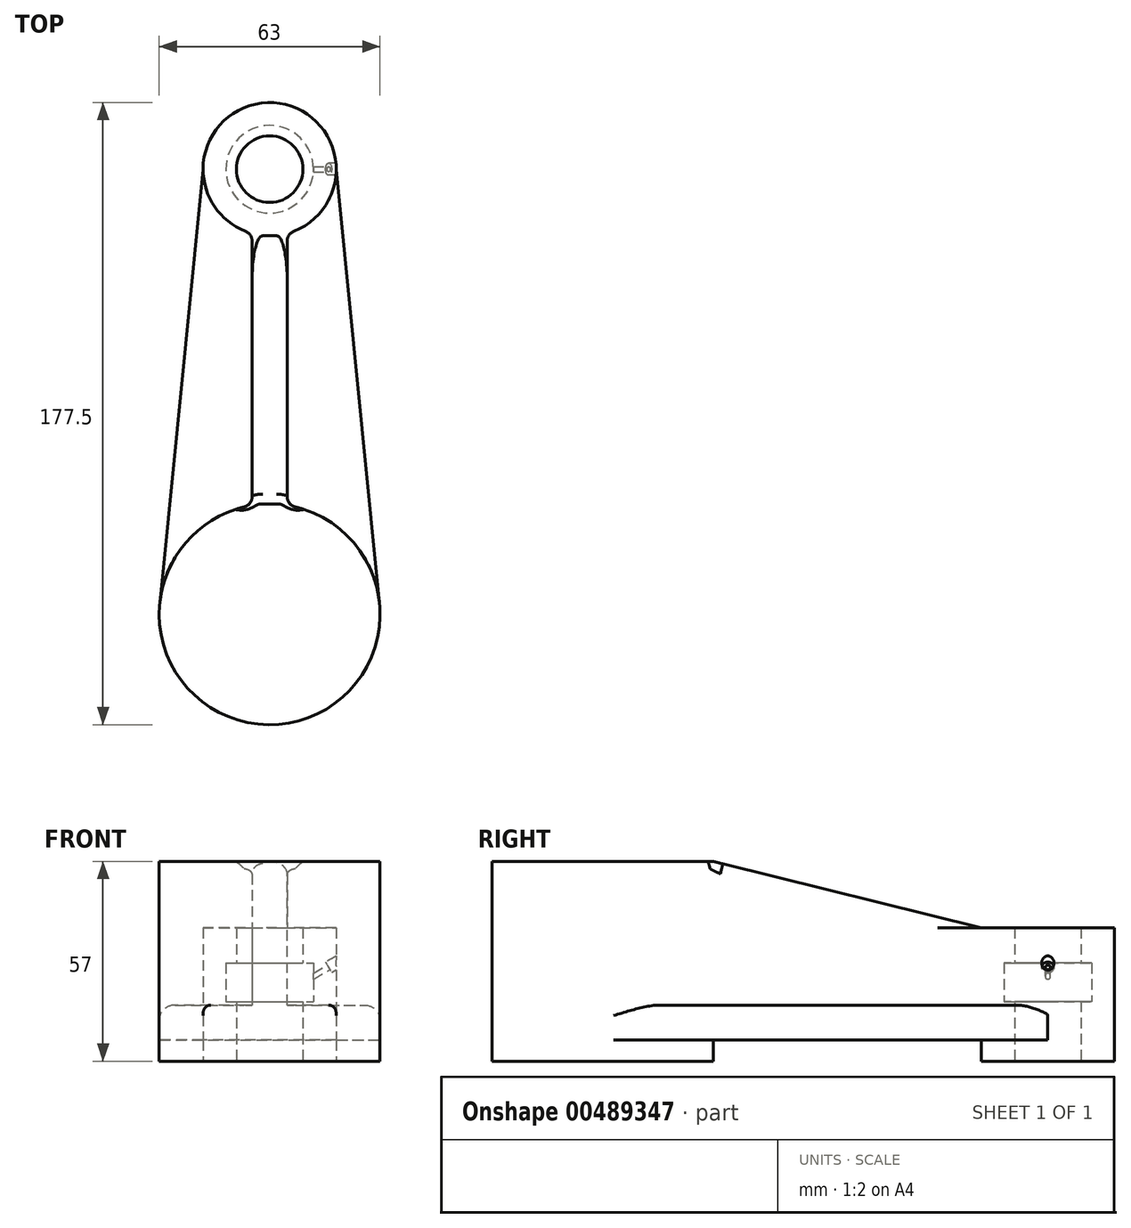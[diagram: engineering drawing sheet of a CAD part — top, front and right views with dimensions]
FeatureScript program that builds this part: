
annotation { "Feature Type Name" : "Feature", "Feature Type Description" : "" }
export const myFeature = defineFeature(function(context is Context, id is Id, definition is map)
    precondition{}
    {
        {
            var Q0;
            Q0=qCreatedBy(makeId("Right.planeOp"),FACE);
            var sketch = newSketch(context, id + "F0", { "sketchPlane" : qUnion([Q0])});
            skLineSegment(sketch, "E0.bottom", {"start": v(0, 0) * mm, "end": v(-19, 0) * mm});
            skLineSegment(sketch, "E0.top", {"start": v(0, 38) * mm, "end": v(-19, 38) * mm});
            skLineSegment(sketch, "E0.right", {"start": v(-19, 0) * mm, "end": v(-19, 38) * mm});
            skLineSegment(sketch, "E1.bottom", {"start": v(-9.5, 28) * mm, "end": v(-12.5, 28) * mm});
            skLineSegment(sketch, "E1.top", {"start": v(-9.5, 17) * mm, "end": v(-12.5, 17) * mm});
            skLineSegment(sketch, "E1.right", {"start": v(-12.5, 28) * mm, "end": v(-12.5, 17) * mm});
            skLineSegment(sketch, "E2.right", {"start": v(-9.5, 0) * mm, "end": v(-9.5, 17) * mm});
            skLineSegment(sketch, "E3.trimOffspring", {"start": v(-9.5, 28) * mm, "end": v(-9.5, 38) * mm});
            skLineSegment(sketch, "E4", {"start": v(0, 0) * mm, "end": v(0, 38) * mm});
            skLineSegment(sketch, "E5", {"start": v(0, 6) * mm, "end": v(-127, 6) * mm});
            skLineSegment(sketch, "E6.bottom", {"start": v(-127, 0) * mm, "end": v(-95.5, 0) * mm});
            skLineSegment(sketch, "E6.top", {"start": v(-127, 57) * mm, "end": v(-95.5, 57) * mm});
            skLineSegment(sketch, "E6.left", {"start": v(-127, 0) * mm, "end": v(-127, 57) * mm});
            skLineSegment(sketch, "E6.right", {"start": v(-95.5, 0) * mm, "end": v(-95.5, 57) * mm});
            skLineSegment(sketch, "E7", {"start": v(-95.5, 57) * mm, "end": v(-19, 38) * mm});
            skLineSegment(sketch, "E8.bottom", {"start": v(-127, 0) * mm, "end": v(-108, 0) * mm});
            skLineSegment(sketch, "E8.top", {"start": v(-127, 57) * mm, "end": v(-108, 57) * mm});
            skLineSegment(sketch, "E8.left", {"start": v(-127, 0) * mm, "end": v(-127, 57) * mm, "construction": true});
            skLineSegment(sketch, "E8.right", {"start": v(-108, 0) * mm, "end": v(-108, 57) * mm});
            skSolve(sketch);
        }
        {
            var Q0;
            {var subQ5=sQuery(id+"F0.wireOp",EDGE,"E6.top");Q0=makeQuery(id+"F0.imprint","IMPRINT",FACE,{"disambiguationData":[TD([[makeQuery(id+"F0.imprint","IMPRINT",EDGE,{"derivedFrom":subQ5}),-1.0]])]});}
            var Q1;
            {var subQ5=sQuery(id+"F0.wireOp",EDGE,"E6.bottom");Q1=makeQuery(id+"F0.imprint","IMPRINT",FACE,{"disambiguationData":[TD([[makeQuery(id+"F0.imprint","IMPRINT",EDGE,{"derivedFrom":subQ5}),1.0]])]});}
            var Q2;
            Q2=sQuery(id+"F0.wireOp",EDGE,"E6.left");
            revolve(context, id + "F1", {"entities" : qUnion([Q0, Q1]), "axis" : qUnion([Q2]), "revolveType" : RevolveType.FULL});
        }
        {
            var Q0;
            {var subQ5=sQuery(id+"F0.wireOp",EDGE,"E6.top");Q0=makeQuery(id+"F0.imprint","IMPRINT",FACE,{"disambiguationData":[TD([[makeQuery(id+"F0.imprint","IMPRINT",EDGE,{"derivedFrom":subQ5}),-1.0]])]});}
            var Q1;
            {var subQ0=sQuery(id+"F0.wireOp",EDGE,"E7");Q1=makeQuery(id+"F0.imprint","IMPRINT",FACE,{"disambiguationData":[TD([[makeQuery(id+"F0.imprint","IMPRINT",EDGE,{"derivedFrom":subQ0}),-1.0]])]});}
            var Q2;
            Q2=makeQuery(id+"F0.imprint","IMPRINT",FACE,{"disambiguationData":[TD([[makeQuery(id+"F0.imprint","IMPRINT",EDGE,{"derivedFrom":sQuery(id+"F0.wireOp",EDGE,"E1.bottom")}),-1.0]])]});
            extrude(context, id + "F2", {"entities" : qUnion([Q0, Q1, Q2]), "operationType" : NewBodyOperationType.ADD, "endBound" : BoundingType.SYMMETRIC, "depth" : 10 * mm, "offsetDistance" : 25 * mm});
        }
        {
            var Q0;
            Q0=makeQuery(id+"F0.imprint","IMPRINT",FACE,{"disambiguationData":[TD([[makeQuery(id+"F0.imprint","IMPRINT",EDGE,{"derivedFrom":sQuery(id+"F0.wireOp",EDGE,"E1.bottom")}),-1.0]])]});
            var Q1;
            {var subQ0=sQuery(id+"F0.wireOp",EDGE,"E0.right");var subQ1=sQuery(id+"F0.wireOp",EDGE,"E0.bottom");var subQ2=makeQuery(id+"F0.imprint","INTERSECT",VERTEX,{"derivedFrom":[subQ1,subQ0]});Q1=makeQuery(id+"F0.imprint","IMPRINT",FACE,{"disambiguationData":[TD([[makeQuery(id+"F0.imprint","IMPRINT",EDGE,{"disambiguationData":[TD([[subQ2,1.0]])],"derivedFrom":subQ1}),-1.0]])]});}
            var Q2;
            Q2=sQuery(id+"F0.wireOp",EDGE,"E4");
            revolve(context, id + "F3", {"operationType" : NewBodyOperationType.ADD, "entities" : qUnion([Q0, Q1]), "axis" : qUnion([Q2]), "revolveType" : RevolveType.FULL});
        }
        {
            var Q0;
            Q0=qCreatedBy(makeId("Right.planeOp"),FACE);
            cPlane(context, id + "F4", {"entities" : qUnion([Q0]), "cplaneType" : CPlaneType.OFFSET, "offset" : 19 * mm, "width" : 150 * mm, "height" : 150 * mm});
        }
        {
            var Q0;
            Q0=qCreatedBy(id+"F4.planeOp",FACE);
            var sketch = newSketch(context, id + "F5", { "sketchPlane" : qUnion([Q0])});
            skLineSegment(sketch, "E9.0", {"start": v(9.5, 28) * mm, "end": v(-9.5, 28) * mm});
            skSolve(sketch);
        }
        {
            var Q0;
            Q0=sQuery(id+"F5.wireOp",EDGE,"E9.0");
            cPlane(context, id + "F6", {"entities" : qUnion([Q0]), "cplaneType" : CPlaneType.LINE_ANGLE, "offset" : 25 * mm, "angle" : 300 * degree, "width" : 150 * mm, "height" : 150 * mm});
        }
        {
            var Q0;
            Q0=qCreatedBy(id+"F6.planeOp",FACE);
            var sketch = newSketch(context, id + "F7", { "sketchPlane" : qUnion([Q0])});
            skCircle(sketch, "E10", {"center": v(0, 14.75) * mm, "radius": 1.75 * mm});
            skCircle(sketch, "E11", {"center": v(0, 14.75) * mm, "radius": 0.75 * mm});
            skLineSegment(sketch, "E12.0", {"start": v(-9.5, 14.75) * mm, "end": v(9.5, 14.75) * mm});
            skSolve(sketch);
        }
        {
            var Q0;
            Q0 = qSketchRegion(id + "F7", true);
            extrude(context, id + "F8", {"entities" : qUnion([Q0]), "operationType" : NewBodyOperationType.REMOVE, "endBound" : BoundingType.SYMMETRIC, "oppositeDirection" : true, "depth" : 5 * mm, "offsetDistance" : 25 * mm});
        }
        {
            var Q0;
            {var subQ0=sQuery(id+"F7.wireOp",EDGE,"E12.0");var subQ1=sQuery(id+"F7.wireOp",EDGE,"E11");var subQ2=makeQuery(id+"F7.imprint","INTERSECT",VERTEX,{"disambiguationData":[OD(0.0)],"derivedFrom":[subQ1,subQ0]});Q0=makeQuery(id+"F7.imprint","IMPRINT",FACE,{"disambiguationData":[TD([[makeQuery(id+"F7.imprint","IMPRINT",EDGE,{"disambiguationData":[TD([[subQ2,-1.0]])],"derivedFrom":subQ1}),1.0]])]});}
            var Q1;
            {var subQ0=sQuery(id+"F7.wireOp",EDGE,"E12.0");var subQ1=sQuery(id+"F7.wireOp",EDGE,"E11");var subQ2=makeQuery(id+"F7.imprint","INTERSECT",VERTEX,{"disambiguationData":[OD(0.0)],"derivedFrom":[subQ1,subQ0]});Q1=makeQuery(id+"F7.imprint","IMPRINT",FACE,{"disambiguationData":[TD([[makeQuery(id+"F7.imprint","IMPRINT",EDGE,{"disambiguationData":[TD([[subQ2,1.0]])],"derivedFrom":subQ1}),1.0]])]});}
            extrude(context, id + "F9", {"entities" : qUnion([Q0, Q1]), "operationType" : NewBodyOperationType.REMOVE, "endBound" : BoundingType.SYMMETRIC, "depth" : 25 * mm, "offsetDistance" : 25 * mm});
        }
        {
            var Q0;
            Q0=makeQuery(id+"F2.opExtrude","SWEPT_FACE",FACE,{"disambiguationData":[OSD([sQuery(id+"F0.wireOp",EDGE,"E5")])]});
            var sketch = newSketch(context, id + "F10", { "sketchPlane" : qUnion([Q0])});
            skCircle(sketch, "E13.0", {"center": v(0, 0) * mm, "radius": 19 * mm});
            skCircle(sketch, "E14.0", {"center": v(0, 127) * mm, "radius": 31.5 * mm});
            skLineSegment(sketch, "E15", {"start": v(19, 0) * mm, "end": v(31.34, 123.88) * mm});
            skLineSegment(sketch, "E16", {"start": v(-19, 0) * mm, "end": v(-31.34, 123.88) * mm});
            skSolve(sketch);
        }
        {
            var Q0;
            {var subQ2=sQuery(id+"F10.wireOp",EDGE,"E15");Q0=makeQuery(id+"F10.imprint","IMPRINT",FACE,{"disambiguationData":[TD([[makeQuery(id+"F10.imprint","IMPRINT",EDGE,{"derivedFrom":subQ2}),1.0]])]});}
            var Q1;
            {var subQ2=sQuery(id+"F10.wireOp",EDGE,"E16");Q1=makeQuery(id+"F10.imprint","IMPRINT",FACE,{"disambiguationData":[TD([[makeQuery(id+"F10.imprint","IMPRINT",EDGE,{"derivedFrom":subQ2}),-1.0]])]});}
            extrude(context, id + "F11", {"entities" : qUnion([Q0, Q1]), "operationType" : NewBodyOperationType.ADD, "oppositeDirection" : true, "depth" : 10 * mm, "offsetDistance" : 25 * mm});
        }
        {
            var Q0;
            Q0=makeQuery(id+"F11.opExtrude","CAP_EDGE",EDGE,{"disambiguationData":[OSD([sQuery(id+"F10.wireOp",EDGE,"E15")])],"isStart":false});
            var Q1;
            {var subQ0=sQuery(id+"F0.wireOp",EDGE,"E5");Q1=makeQuery(id+"F11.opExtrude","CAP_EDGE",EDGE,{"disambiguationData":[OSD([subQ0]),TDD([makeQuery(id+"F10.imprint","IMPRINT",EDGE,{"derivedFrom":makeQuery(id+"F2.opExtrude","CAP_EDGE",EDGE,{"disambiguationData":[OSD([subQ0])],"isStart":false})})])],"isStart":false});}
            var Q2;
            {var subQ0=sQuery(id+"F10.wireOp",EDGE,"E14.0");Q2=makeQuery(id+"F11.opExtrude","CAP_EDGE",EDGE,{"disambiguationData":[OSD([subQ0]),TDD([makeQuery(id+"F10.imprint","IMPRINT",EDGE,{"disambiguationData":[TD([[makeQuery(id+"F10.imprint","INTERSECT",VERTEX,{"derivedFrom":[makeQuery(id+"F2.opExtrude","CAP_EDGE",EDGE,{"disambiguationData":[OSD([sQuery(id+"F0.wireOp",EDGE,"E5")])],"isStart":false}),subQ0]}),-1.0],[makeQuery(id+"F10.imprint","INTERSECT",VERTEX,{"derivedFrom":[subQ0,sQuery(id+"F10.wireOp",EDGE,"E15")]}),1.0]])],"derivedFrom":subQ0})])],"isStart":false});}
            var Q3;
            Q3=makeQuery(id+"F2.boolean.opBoolean","INTERSECT",EDGE,{"derivedFrom":[makeQuery(id+"F1.opRevolve","SWEPT_FACE",FACE,{"disambiguationData":[OSD([sQuery(id+"F0.wireOp",EDGE,"E6.right")])]}),makeQuery(id+"F2.opExtrude","CAP_FACE",FACE,{"disambiguationData":[OSD([sQuery(id+"F0.wireOp",EDGE,"E0.top"),sQuery(id+"F0.wireOp",EDGE,"E1.bottom"),sQuery(id+"F0.wireOp",EDGE,"E1.top"),sQuery(id+"F0.wireOp",EDGE,"E1.right"),sQuery(id+"F0.wireOp",EDGE,"E2.right"),sQuery(id+"F0.wireOp",EDGE,"E3.trimOffspring"),sQuery(id+"F0.wireOp",EDGE,"E5"),sQuery(id+"F0.wireOp",EDGE,"E6.top"),sQuery(id+"F0.wireOp",EDGE,"E7"),sQuery(id+"F0.wireOp",EDGE,"E8.right")])],"isStart":false})]});
            var Q4;
            Q4=makeQuery(id+"F3.boolean.opBoolean","INTERSECT",EDGE,{"derivedFrom":[makeQuery(id+"F2.opExtrude","CAP_FACE",FACE,{"disambiguationData":[OSD([sQuery(id+"F0.wireOp",EDGE,"E0.top"),sQuery(id+"F0.wireOp",EDGE,"E1.bottom"),sQuery(id+"F0.wireOp",EDGE,"E1.top"),sQuery(id+"F0.wireOp",EDGE,"E1.right"),sQuery(id+"F0.wireOp",EDGE,"E2.right"),sQuery(id+"F0.wireOp",EDGE,"E3.trimOffspring"),sQuery(id+"F0.wireOp",EDGE,"E5"),sQuery(id+"F0.wireOp",EDGE,"E6.top"),sQuery(id+"F0.wireOp",EDGE,"E7"),sQuery(id+"F0.wireOp",EDGE,"E8.right")])],"isStart":false}),makeQuery(id+"F3.opRevolve","SWEPT_FACE",FACE,{"disambiguationData":[OSD([sQuery(id+"F0.wireOp",EDGE,"E0.right")])]})]});
            var Q5;
            Q5=makeQuery(id+"F3.boolean.opBoolean","INTERSECT",EDGE,{"derivedFrom":[makeQuery(id+"F2.opExtrude","CAP_FACE",FACE,{"disambiguationData":[OSD([sQuery(id+"F0.wireOp",EDGE,"E0.top"),sQuery(id+"F0.wireOp",EDGE,"E1.bottom"),sQuery(id+"F0.wireOp",EDGE,"E1.top"),sQuery(id+"F0.wireOp",EDGE,"E1.right"),sQuery(id+"F0.wireOp",EDGE,"E2.right"),sQuery(id+"F0.wireOp",EDGE,"E3.trimOffspring"),sQuery(id+"F0.wireOp",EDGE,"E5"),sQuery(id+"F0.wireOp",EDGE,"E6.top"),sQuery(id+"F0.wireOp",EDGE,"E7"),sQuery(id+"F0.wireOp",EDGE,"E8.right")])],"isStart":true}),makeQuery(id+"F3.opRevolve","SWEPT_FACE",FACE,{"disambiguationData":[OSD([sQuery(id+"F0.wireOp",EDGE,"E0.right")])]})]});
            var Q6;
            {var subQ0=sQuery(id+"F0.wireOp",EDGE,"E5");Q6=makeQuery(id+"F11.opExtrude","CAP_EDGE",EDGE,{"disambiguationData":[OSD([subQ0]),TDD([makeQuery(id+"F10.imprint","IMPRINT",EDGE,{"derivedFrom":makeQuery(id+"F2.opExtrude","CAP_EDGE",EDGE,{"disambiguationData":[OSD([subQ0])],"isStart":true})})])],"isStart":false});}
            var Q7;
            Q7=makeQuery(id+"F2.boolean.opBoolean","INTERSECT",EDGE,{"derivedFrom":[makeQuery(id+"F1.opRevolve","SWEPT_FACE",FACE,{"disambiguationData":[OSD([sQuery(id+"F0.wireOp",EDGE,"E6.right")])]}),makeQuery(id+"F2.opExtrude","CAP_FACE",FACE,{"disambiguationData":[OSD([sQuery(id+"F0.wireOp",EDGE,"E0.top"),sQuery(id+"F0.wireOp",EDGE,"E1.bottom"),sQuery(id+"F0.wireOp",EDGE,"E1.top"),sQuery(id+"F0.wireOp",EDGE,"E1.right"),sQuery(id+"F0.wireOp",EDGE,"E2.right"),sQuery(id+"F0.wireOp",EDGE,"E3.trimOffspring"),sQuery(id+"F0.wireOp",EDGE,"E5"),sQuery(id+"F0.wireOp",EDGE,"E6.top"),sQuery(id+"F0.wireOp",EDGE,"E7"),sQuery(id+"F0.wireOp",EDGE,"E8.right")])],"isStart":true})]});
            var Q8;
            Q8=makeQuery(id+"F11.opExtrude","CAP_EDGE",EDGE,{"disambiguationData":[OSD([sQuery(id+"F10.wireOp",EDGE,"E16")])],"isStart":false});
            var Q9;
            {var subQ0=sQuery(id+"F10.wireOp",EDGE,"E14.0");Q9=makeQuery(id+"F11.opExtrude","CAP_EDGE",EDGE,{"disambiguationData":[OSD([subQ0]),TDD([makeQuery(id+"F10.imprint","IMPRINT",EDGE,{"disambiguationData":[TD([[makeQuery(id+"F10.imprint","INTERSECT",VERTEX,{"derivedFrom":[makeQuery(id+"F2.opExtrude","CAP_EDGE",EDGE,{"disambiguationData":[OSD([sQuery(id+"F0.wireOp",EDGE,"E5")])],"isStart":true}),subQ0]}),1.0],[makeQuery(id+"F10.imprint","INTERSECT",VERTEX,{"derivedFrom":[subQ0,sQuery(id+"F10.wireOp",EDGE,"E16")]}),-1.0]])],"derivedFrom":subQ0})])],"isStart":false});}
            var Q10;
            {var subQ0=sQuery(id+"F10.wireOp",EDGE,"E13.0");Q10=makeQuery(id+"F11.opExtrude","CAP_EDGE",EDGE,{"disambiguationData":[OSD([subQ0]),TDD([makeQuery(id+"F10.imprint","IMPRINT",EDGE,{"disambiguationData":[TD([[makeQuery(id+"F10.imprint","INTERSECT",VERTEX,{"derivedFrom":[makeQuery(id+"F2.opExtrude","CAP_EDGE",EDGE,{"disambiguationData":[OSD([sQuery(id+"F0.wireOp",EDGE,"E5")])],"isStart":true}),subQ0]}),-1.0]])],"derivedFrom":subQ0})])],"isStart":false});}
            var Q11;
            {var subQ0=sQuery(id+"F10.wireOp",EDGE,"E13.0");Q11=makeQuery(id+"F11.opExtrude","CAP_EDGE",EDGE,{"disambiguationData":[OSD([subQ0]),TDD([makeQuery(id+"F10.imprint","IMPRINT",EDGE,{"disambiguationData":[TD([[makeQuery(id+"F10.imprint","INTERSECT",VERTEX,{"derivedFrom":[makeQuery(id+"F2.opExtrude","CAP_EDGE",EDGE,{"disambiguationData":[OSD([sQuery(id+"F0.wireOp",EDGE,"E5")])],"isStart":false}),subQ0]}),1.0]])],"derivedFrom":subQ0})])],"isStart":false});}
            fillet(context, id + "F12", {"entities" : qUnion([Q0, Q1, Q2, Q3, Q4, Q5, Q6, Q7, Q8, Q9, Q10, Q11]), "radius" : 3 * mm, "tangentPropagation" : true, "allowEdgeOverflow" : false});
        }
        {
            var Q0;
            Q0=makeQuery(id+"F2.opExtrude","CAP_EDGE",EDGE,{"disambiguationData":[OSD([sQuery(id+"F0.wireOp",EDGE,"E7")])],"isStart":false});
            var Q1;
            Q1=makeQuery(id+"F2.opExtrude","CAP_EDGE",EDGE,{"disambiguationData":[OSD([sQuery(id+"F0.wireOp",EDGE,"E7")])],"isStart":true});
            fillet(context, id + "F13", {"entities" : qUnion([Q0, Q1]), "radius" : 3 * mm, "tangentPropagation" : true, "allowEdgeOverflow" : false});
        }
    });
